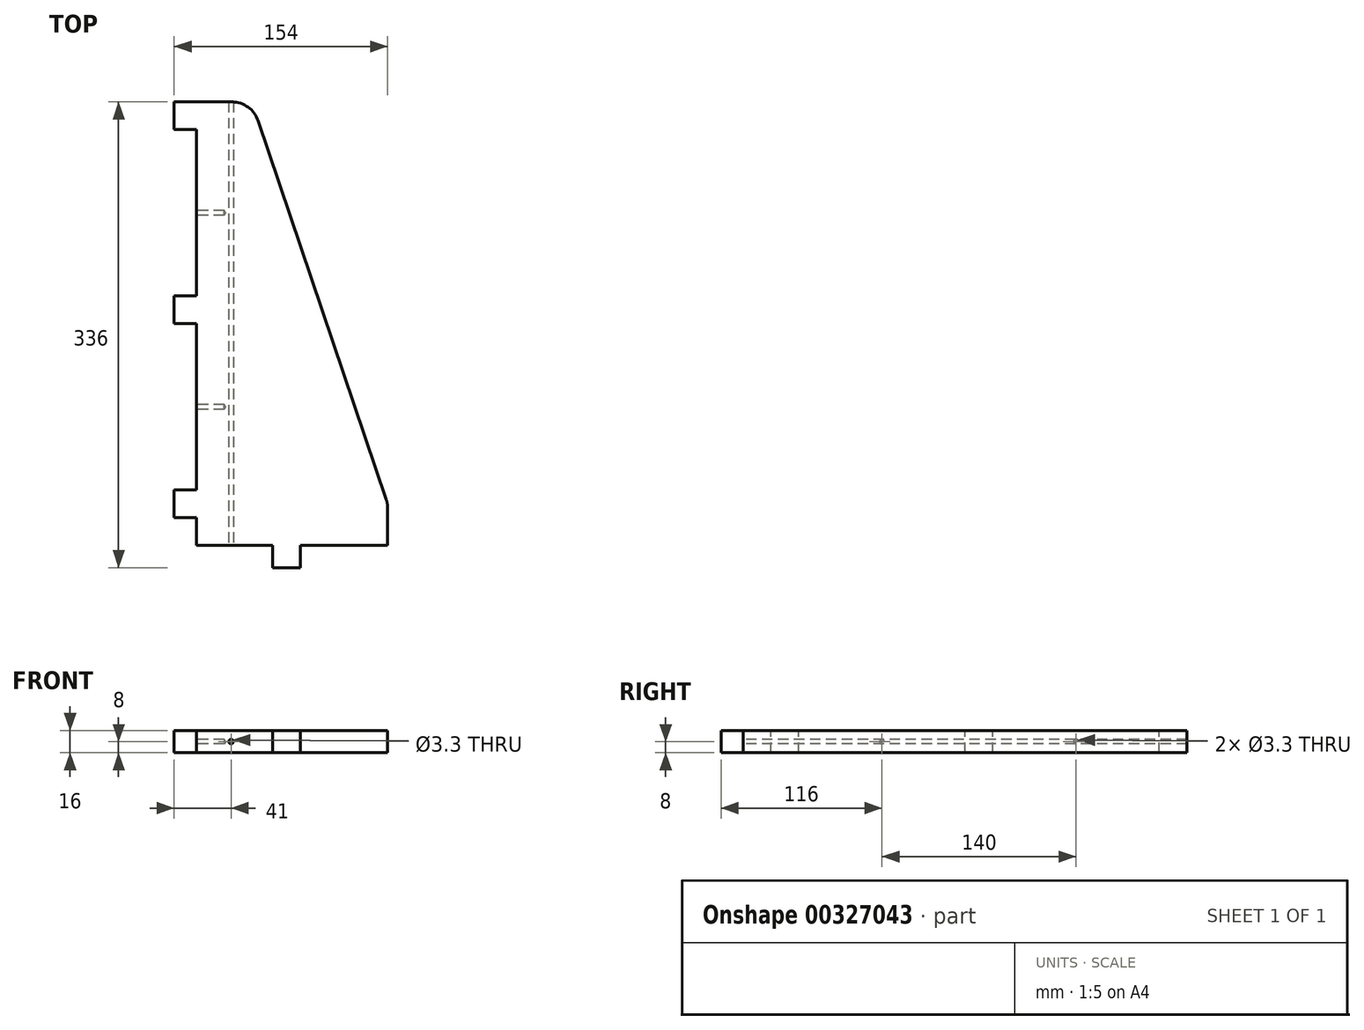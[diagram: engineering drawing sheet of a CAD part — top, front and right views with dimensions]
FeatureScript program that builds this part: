
annotation { "Feature Type Name" : "Feature", "Feature Type Description" : "" }
export const myFeature = defineFeature(function(context is Context, id is Id, definition is map)
    precondition{}
    {
        {
            var Q0;
            Q0=qCreatedBy(makeId("Top.planeOp"),FACE);
            var sketch = newSketch(context, id + "F0", { "sketchPlane" : qUnion([Q0])});
            skLineSegment(sketch, "E0", {"start": v(0, 0) * mm, "end": v(138, 0) * mm});
            skLineSegment(sketch, "E1", {"start": v(138, 30) * mm, "end": v(40, 320) * mm});
            skLineSegment(sketch, "E2", {"start": v(40, 320) * mm, "end": v(0, 320) * mm});
            skLineSegment(sketch, "E3", {"start": v(0, 320) * mm, "end": v(0, 0) * mm});
            skLineSegment(sketch, "E4", {"start": v(138, 30) * mm, "end": v(138, 0) * mm});
            skSolve(sketch);
        }
        {
            var Q0;
            Q0=makeQuery(id+"F0.imprint","IMPRINT",FACE,{"disambiguationData":[TD([[makeQuery(id+"F0.imprint","IMPRINT",EDGE,{"derivedFrom":sQuery(id+"F0.wireOp",EDGE,"E0")}),1.0]])]});
            extrude(context, id + "F1", {"entities" : qUnion([Q0]), "depth" : 16 * mm});
        }
        {
            var Q0;
            Q0=makeQuery(id+"F1.opExtrude","CAP_FACE",FACE,{"disambiguationData":[OSD([sQuery(id+"F0.wireOp",EDGE,"E0"),sQuery(id+"F0.wireOp",EDGE,"E1"),sQuery(id+"F0.wireOp",EDGE,"E2"),sQuery(id+"F0.wireOp",EDGE,"E3")])],"isStart":false});
            var sketch = newSketch(context, id + "F2", { "sketchPlane" : qUnion([Q0])});
            skLineSegment(sketch, "E5", {"start": v(55, 0) * mm, "end": v(55, -16) * mm});
            skLineSegment(sketch, "E6", {"start": v(55, -16) * mm, "end": v(75, -16) * mm});
            skLineSegment(sketch, "E7", {"start": v(75, -16) * mm, "end": v(75, 0) * mm});
            skLineSegment(sketch, "E8", {"start": v(0, 20) * mm, "end": v(-16, 20) * mm});
            skLineSegment(sketch, "E9", {"start": v(-16, 20) * mm, "end": v(-16, 40) * mm});
            skLineSegment(sketch, "E10", {"start": v(-16, 40) * mm, "end": v(0, 40) * mm});
            skLineSegment(sketch, "E11", {"start": v(0, 160) * mm, "end": v(-16, 160) * mm});
            skLineSegment(sketch, "E12", {"start": v(-16, 160) * mm, "end": v(-16, 180) * mm});
            skLineSegment(sketch, "E13", {"start": v(-16, 180) * mm, "end": v(0, 180) * mm});
            skLineSegment(sketch, "E14", {"start": v(0, 300) * mm, "end": v(-16, 300) * mm});
            skLineSegment(sketch, "E15", {"start": v(-16, 300) * mm, "end": v(-16, 320) * mm});
            skLineSegment(sketch, "E16", {"start": v(-16, 320) * mm, "end": v(0, 320) * mm});
            skSolve(sketch);
        }
        {
            var Q0;
            {var subQ0=sQuery(id+"F2.wireOp",EDGE,"E14");Q0=makeQuery(id+"F2.imprint","IMPRINT",FACE,{"disambiguationData":[TD([[makeQuery(id+"F2.imprint","IMPRINT",EDGE,{"derivedFrom":subQ0}),-1.0]])]});}
            var Q1;
            {var subQ0=sQuery(id+"F2.wireOp",EDGE,"E11");Q1=makeQuery(id+"F2.imprint","IMPRINT",FACE,{"disambiguationData":[TD([[makeQuery(id+"F2.imprint","IMPRINT",EDGE,{"derivedFrom":subQ0}),-1.0]])]});}
            var Q2;
            {var subQ0=sQuery(id+"F2.wireOp",EDGE,"E5");Q2=makeQuery(id+"F2.imprint","IMPRINT",FACE,{"disambiguationData":[TD([[makeQuery(id+"F2.imprint","IMPRINT",EDGE,{"derivedFrom":subQ0}),1.0]])]});}
            var Q3;
            {var subQ0=sQuery(id+"F2.wireOp",EDGE,"E8");Q3=makeQuery(id+"F2.imprint","IMPRINT",FACE,{"disambiguationData":[TD([[makeQuery(id+"F2.imprint","IMPRINT",EDGE,{"derivedFrom":subQ0}),-1.0]])]});}
            var Q4;
            Q4=makeQuery(id+"F1.opExtrude","CAP_FACE",FACE,{"disambiguationData":[OSD([sQuery(id+"F0.wireOp",EDGE,"E0"),sQuery(id+"F0.wireOp",EDGE,"E1"),sQuery(id+"F0.wireOp",EDGE,"E2"),sQuery(id+"F0.wireOp",EDGE,"E3")])],"isStart":true});
            extrude(context, id + "F3", {"entities" : qUnion([Q0, Q1, Q2, Q3]), "operationType" : NewBodyOperationType.ADD, "endBound" : BoundingType.UP_TO_SURFACE, "oppositeDirection" : true, "endBoundEntityFace" : qUnion([Q4]), "depth" : 25 * mm});
        }
        {
            var Q0;
            Q0=makeQuery(id+"F1.opExtrude","SWEPT_EDGE",EDGE,{"disambiguationData":[OSD([sQuery(id+"F0.wireOp",EDGE,"E1"),sQuery(id+"F0.wireOp",EDGE,"E2")])]});
            var Q1;
            Q1=makeQuery(id+"F1.opExtrude","SWEPT_EDGE",EDGE,{"disambiguationData":[OSD([sQuery(id+"F0.wireOp",EDGE,"E1"),sQuery(id+"F0.wireOp",EDGE,"E4")])]});
            fillet(context, id + "F4", {"entities" : qUnion([Q0, Q1]), "radius" : 20 * mm, "tangentPropagation" : true, "allowEdgeOverflow" : false});
        }
        {
            var Q0;
            {var subQ0=sQuery(id+"F2.wireOp",EDGE,"E10");var subQ3=sQuery(id+"F0.wireOp",EDGE,"E3");Q0=makeQuery(id+"F3.boolean.opBoolean","SPLIT",FACE,{"disambiguationData":[TD([makeQuery(id+"F3.opExtrude","SWEPT_FACE",FACE,{"disambiguationData":[OSD([subQ0])]})])],"derivedFrom":makeQuery(id+"F1.opExtrude","SWEPT_FACE",FACE,{"disambiguationData":[OSD([subQ3])]})});}
            var sketch = newSketch(context, id + "F5", { "sketchPlane" : qUnion([Q0])});
            skLineSegment(sketch, "E17", {"start": v(-160, 8) * mm, "end": v(-100, 8) * mm});
            skPoint(sketch, "E17.endSnap0", {"position": v(-40, 8) * mm});
            skPoint(sketch, "E18.0", {"position": v(-180, 8) * mm});
            skLineSegment(sketch, "E19", {"start": v(-180, 8) * mm, "end": v(-240, 8) * mm});
            skSolve(sketch);
        }
        {
            var Q0;
            Q0=sQuery(id+"F5.wireOp",VERTEX,"E19.end");
            var Q1;
            Q1=sQuery(id+"F5.wireOp",VERTEX,"E17.end");
            var Q2;
            Q2=makeQuery(id+"F1.opExtrude","SWEPT_BODY",BODY,{"disambiguationData":[OSD([sQuery(id+"F0.wireOp",EDGE,"E0"),sQuery(id+"F0.wireOp",EDGE,"E1"),sQuery(id+"F0.wireOp",EDGE,"E2"),sQuery(id+"F0.wireOp",EDGE,"E3"),sQuery(id+"F0.wireOp",EDGE,"E4")])]});
            hole(context, id + "F6", {"style" : HoleStyle.SIMPLE, "endStyle" : HoleEndStyle.BLIND, "standardTappedOrClearance" : lookupTablePath({ "standard" : "ISO", "fit" : "Normal", "size" : "M3", "type" : "Clearance" }), "standardBlindInLast" : lookupTablePath({ "fit" : "Standard", "standard" : "ISO", "size" : "M3", "type" : "Clearance" }), "holeDiameter" : 3.3 * mm, "holeDepth" : 20 * mm, "tappedDepth" : 12 * mm, "tapClearance" : 3, "locations" : qUnion([Q0, Q1]), "scope" : qUnion([Q2])});
        }
        {
            var Q0;
            {var subQ3=sQuery(id+"F0.wireOp",EDGE,"E3");var subQ7=sQuery(id+"F0.wireOp",EDGE,"E0");Q0=makeQuery(id+"F3.boolean.opBoolean","SPLIT",FACE,{"disambiguationData":[TD([makeQuery(id+"F1.opExtrude","SWEPT_FACE",FACE,{"disambiguationData":[OSD([subQ3])]})])],"derivedFrom":makeQuery(id+"F1.opExtrude","SWEPT_FACE",FACE,{"disambiguationData":[OSD([subQ7])]})});}
            var sketch = newSketch(context, id + "F7", { "sketchPlane" : qUnion([Q0])});
            skLineSegment(sketch, "E20", {"start": v(55, 8) * mm, "end": v(25, 8) * mm});
            skSolve(sketch);
        }
        {
            var Q0;
            Q0=sQuery(id+"F7.wireOp",VERTEX,"E20.end");
            var Q1;
            Q1=makeQuery(id+"F1.opExtrude","SWEPT_BODY",BODY,{"disambiguationData":[OSD([sQuery(id+"F0.wireOp",EDGE,"E0"),sQuery(id+"F0.wireOp",EDGE,"E1"),sQuery(id+"F0.wireOp",EDGE,"E2"),sQuery(id+"F0.wireOp",EDGE,"E3"),sQuery(id+"F0.wireOp",EDGE,"E4")])]});
            hole(context, id + "F8", {"style" : HoleStyle.SIMPLE, "endStyle" : HoleEndStyle.THROUGH, "standardTappedOrClearance" : lookupTablePath({ "standard" : "ISO", "fit" : "Normal", "size" : "M3", "type" : "Clearance" }), "standardBlindInLast" : lookupTablePath({ "fit" : "Standard", "standard" : "ISO", "size" : "M3", "type" : "Clearance" }), "holeDiameter" : 3.3 * mm, "tappedDepth" : 12 * mm, "tapClearance" : 3, "locations" : qUnion([Q0]), "scope" : qUnion([Q1])});
        }
    });
